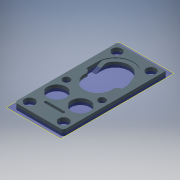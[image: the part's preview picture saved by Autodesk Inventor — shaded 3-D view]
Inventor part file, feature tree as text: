
AUTODESK INVENTOR PART (.ipt)
format: ipt  version: 2016 (Build 200138000, 138)  size: 476,672 bytes
history: native  units: mm
features: extrude x10, sketch x9, projected_geometry x9, chamfer x5, thicken_offset x3, reference x3, plane x2, fillet x2, hole x1
ambient origin geometry x8: Origin, YZ Plane, XZ Plane, XY Plane, X Axis, Y Axis, Z Axis, Center Point
bodies: Solid1 (feature_tree)
feature tree (44):
  sketch  "Sketch2"  dims[d6=10.0mm d7=0.0mm d8=31.25mm]
  plane  "Work Plane3"
  extrude  "Extrusion1"  Depth=31.25mm
  extrude  "Extrusion2"  Depth=14.0mm
  plane  "Work Plane2"
  extrude  "Extrusion3"  TaperAngle=0.0deg  [1 undecoded]
  extrude  "Extrusion4"  Depth=82.0mm
  extrude  "Extrusion5"  Depth=31.25mm
  extrude  "Extrusion6"  TaperAngle=0.0deg  [1 undecoded]
  chamfer  "Chamfer1"  [1 undecoded]
  chamfer  "Chamfer2"  Distance=3.0mm
  extrude  "Extrusion10"  TaperAngle=0.0deg  [1 undecoded]
  extrude  "Extrusion11"  Depth=8.4mm
  chamfer  "Chamfer4"  Distance=3.0mm
  extrude  "Extrusion7"  TaperAngle=45.0deg  [1 undecoded]
  chamfer  "Chamfer3"  Distance=8.4mm
  hole  "Hole1"  [1 undecoded]
  thicken_offset  "Thicken2"
  thicken_offset  "Thicken3"
  extrude  "Extrusion9"  TaperAngle=45.0deg  [1 undecoded]
  chamfer  "Chamfer5"  Distance=6.0mm
  fillet  "Fillet2"  Radius=3.0mm
  fillet  "Fillet3"  [1 undecoded]
  thicken_offset  "Thicken4"
  sketch  "Sketch3"  dims[d9=14.0mm d10=14.0mm]
  sketch  "Sketch4"  dims[d11=3.0mm d12=0.0mm]
  sketch  "Sketch5"  dims[d13=-6.0mm d14=82.0mm]
  sketch  "Sketch6"  dims[d15=14.0mm d16=31.25mm]
  sketch  "Sketch7"  dims[d17=3.0mm d18=0.0mm]
  sketch  "Sketch8"  dims[d20=3.0mm]
  reference  "Reference24"
  sketch  "Sketch11"  dims[d21=0.0mm]
  sketch  "Sketch13"  dims[d23=3.0mm d24=0.0mm d25=3.0mm d26=0.0mm d27=8.4mm d28=3.0mm d29=45.0deg d30=8.4mm d31=3.0mm d32=45.0deg d33=6.0mm d34=3.0mm d35=0.0mm d36=1.5mm d37=3.0mm d38=45.0deg d47=3.0mm d48=6.0mm d49=4.0mm d50=2.0mm d51=90.0deg d52=8.0mm d53=20.594885mm d87=3.0mm d88=0.0mm d89=0.75mm d90=3.0mm d91=45.0deg d93=9.0mm d95=10.0mm d96=0.0mm d97=10.0mm d98=0.0mm d99=3.0mm d100=3.0mm d101=41.0mm d103=1.4mm d104=1.4mm d106=1.4mm d107=0.7mm d109=6.0mm d110=6.0mm d111=2.0mm d112=45.0deg d113=5.585054mm d114=0.6mm d115=12.0mm d116=0.5mm d117=0.5mm]
  projected_geometry  "Projected Loop4"
  projected_geometry  "Projected Loop5"
  projected_geometry  "Projected Loop8"
  reference  "Reference26"
  projected_geometry  "Projected Loop9"
  projected_geometry  "Projected Loop15"
  reference  "Reference27"
  projected_geometry  "Projected Loop17"
  projected_geometry  "Projected Loop18"
  projected_geometry  "Projected Loop19"
  projected_geometry  "Projected Loop20"
note: 8 required parameter values undecoded (feature->parameter linkage not recoverable at this tier; creation-order binding heuristic only, values carry confidence <= 0.55)
